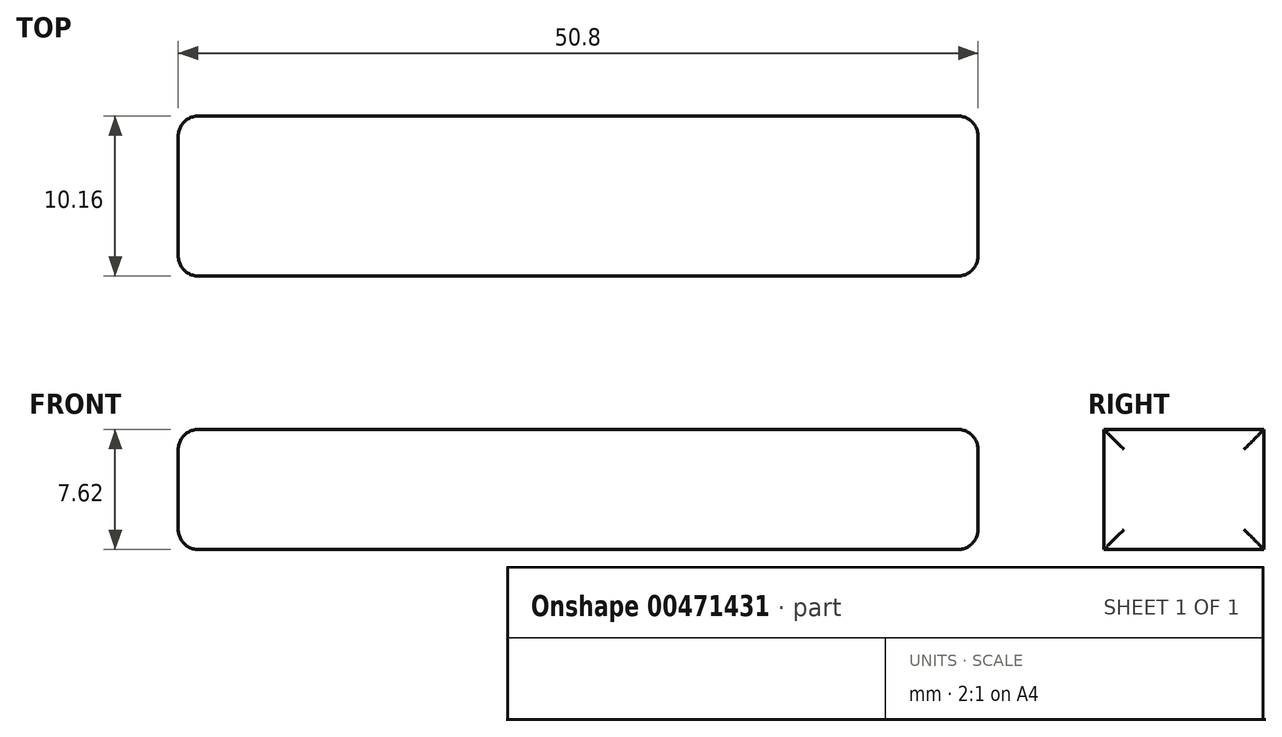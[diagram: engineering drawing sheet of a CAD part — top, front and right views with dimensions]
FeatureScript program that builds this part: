
annotation { "Feature Type Name" : "Feature", "Feature Type Description" : "" }
export const myFeature = defineFeature(function(context is Context, id is Id, definition is map)
    precondition{}
    {
        {
            var Q0;
            Q0=qCreatedBy(makeId("Front.planeOp"),FACE);
            var sketch = newSketch(context, id + "F0", { "sketchPlane" : qUnion([Q0])});
            skLineSegment(sketch, "E0.bottom", {"start": v(-50.8, 7.62) * mm, "end": v(0, 7.62) * mm});
            skLineSegment(sketch, "E0.top", {"start": v(-50.8, 0) * mm, "end": v(0, 0) * mm});
            skLineSegment(sketch, "E0.left", {"start": v(-50.8, 7.62) * mm, "end": v(-50.8, 0) * mm});
            skLineSegment(sketch, "E0.right", {"start": v(0, 7.62) * mm, "end": v(0, 0) * mm});
            skSolve(sketch);
        }
        {
            var Q0;
            Q0 = qSketchRegion(id + "F0", true);
            extrude(context, id + "F1", {"entities" : qUnion([Q0]), "depth" : 10.16 * mm});
        }
        {
            var Q0;
            Q0=makeQuery(id+"F1.opExtrude","SWEPT_FACE",FACE,{"disambiguationData":[OSD([sQuery(id+"F0.wireOp",EDGE,"E0.right")])]});
            var Q1;
            Q1=makeQuery(id+"F1.opExtrude","SWEPT_FACE",FACE,{"disambiguationData":[OSD([sQuery(id+"F0.wireOp",EDGE,"E0.left")])]});
            fillet(context, id + "F2", {"entities" : qUnion([Q0, Q1]), "radius" : 1.27 * mm, "tangentPropagation" : true, "allowEdgeOverflow" : false});
        }
    });
